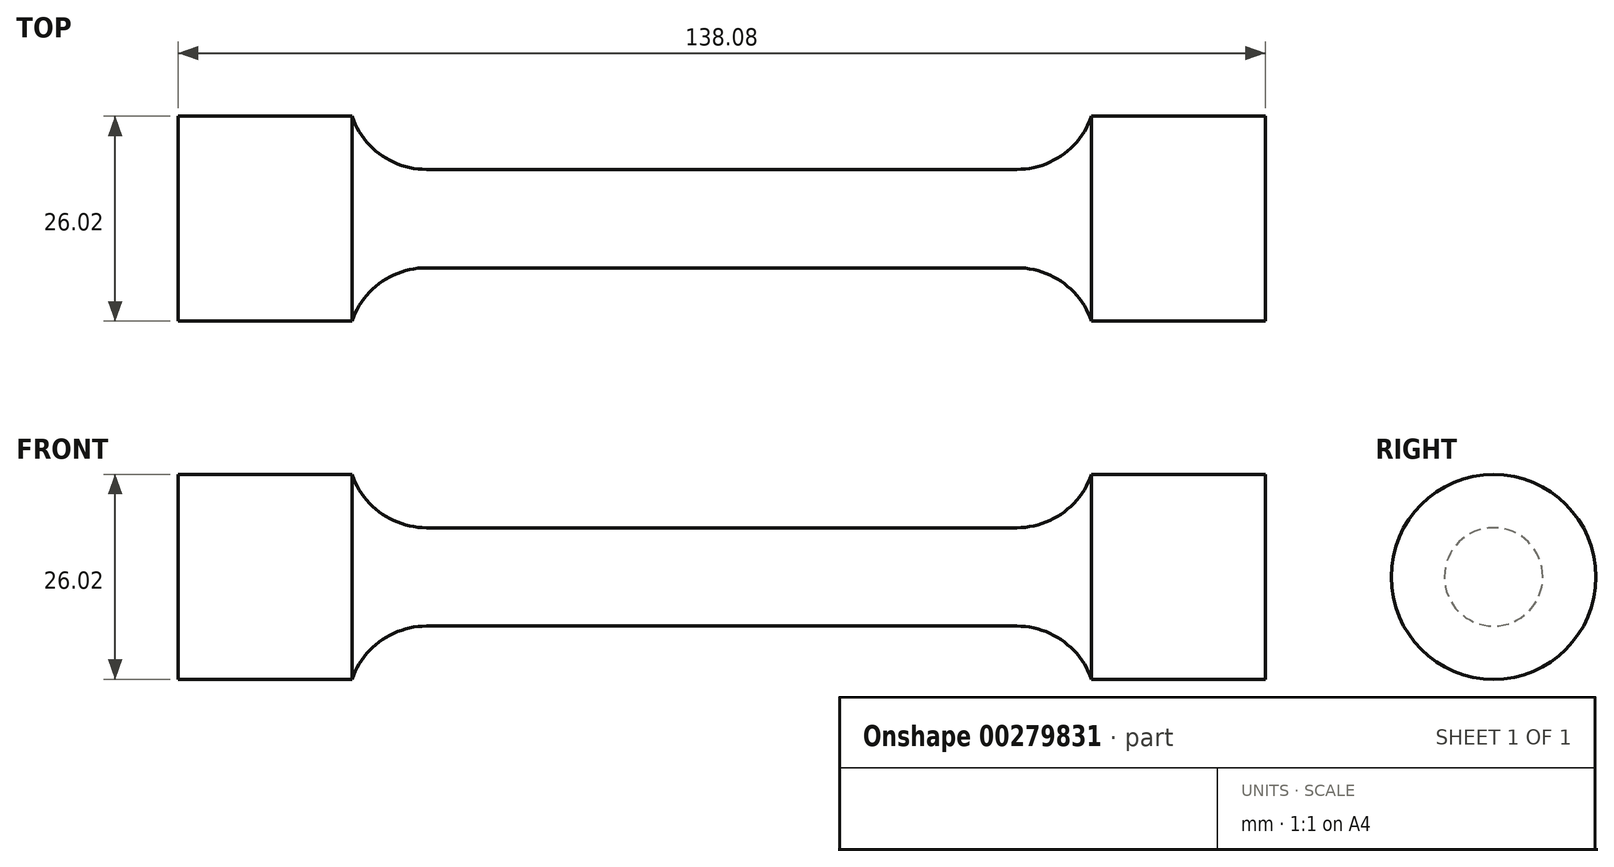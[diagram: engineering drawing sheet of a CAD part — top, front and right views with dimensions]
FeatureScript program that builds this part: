
annotation { "Feature Type Name" : "Feature", "Feature Type Description" : "" }
export const myFeature = defineFeature(function(context is Context, id is Id, definition is map)
    precondition{}
    {
        {
            var Q0;
            Q0=qCreatedBy(makeId("Front.planeOp"),FACE);
            var sketch = newSketch(context, id + "F0", { "sketchPlane" : qUnion([Q0])});
            skLineSegment(sketch, "E0", {"start": v(0, 6.25) * mm, "end": v(37.5, 6.25) * mm});
            skArc(sketch, "E1", {"start": v(37.5, 6.25) * mm, "mid": v(43.31, 8.11) * mm, "end": v(46.96, 13) * mm});
            skLineSegment(sketch, "E2", {"start": v(46.96, 13) * mm, "end": v(69.04, 13) * mm});
            skLineSegment(sketch, "E3", {"start": v(69.04, 13) * mm, "end": v(69.04, 0) * mm});
            skLineSegment(sketch, "E4.MirrorCS", {"start": v(0, 6.25) * mm, "end": v(-37.5, 6.25) * mm});
            skLineSegment(sketch, "E5.MirrorCS", {"start": v(-46.96, 13) * mm, "end": v(-69.04, 13) * mm});
            skArc(sketch, "E6.MirrorCS", {"start": v(-37.5, 6.25) * mm, "mid": v(-43.31, 8.11) * mm, "end": v(-46.96, 13) * mm});
            skLineSegment(sketch, "E7.MirrorCS", {"start": v(-69.04, 13) * mm, "end": v(-69.04, 0) * mm});
            skLineSegment(sketch, "E8", {"start": v(-69.04, 0) * mm, "end": v(69.04, 0) * mm});
            skSolve(sketch);
        }
        {
            var Q0;
            Q0=makeQuery(id+"F0.imprint","IMPRINT",FACE,{"disambiguationData":[TD([[makeQuery(id+"F0.imprint","IMPRINT",EDGE,{"derivedFrom":sQuery(id+"F0.wireOp",EDGE,"E0")}),-1.0]])]});
            var Q1;
            Q1=sQuery(id+"F0.wireOp",EDGE,"E8");
            revolve(context, id + "F1", {"entities" : qUnion([Q0]), "axis" : qUnion([Q1]), "revolveType" : RevolveType.FULL});
        }
    });
